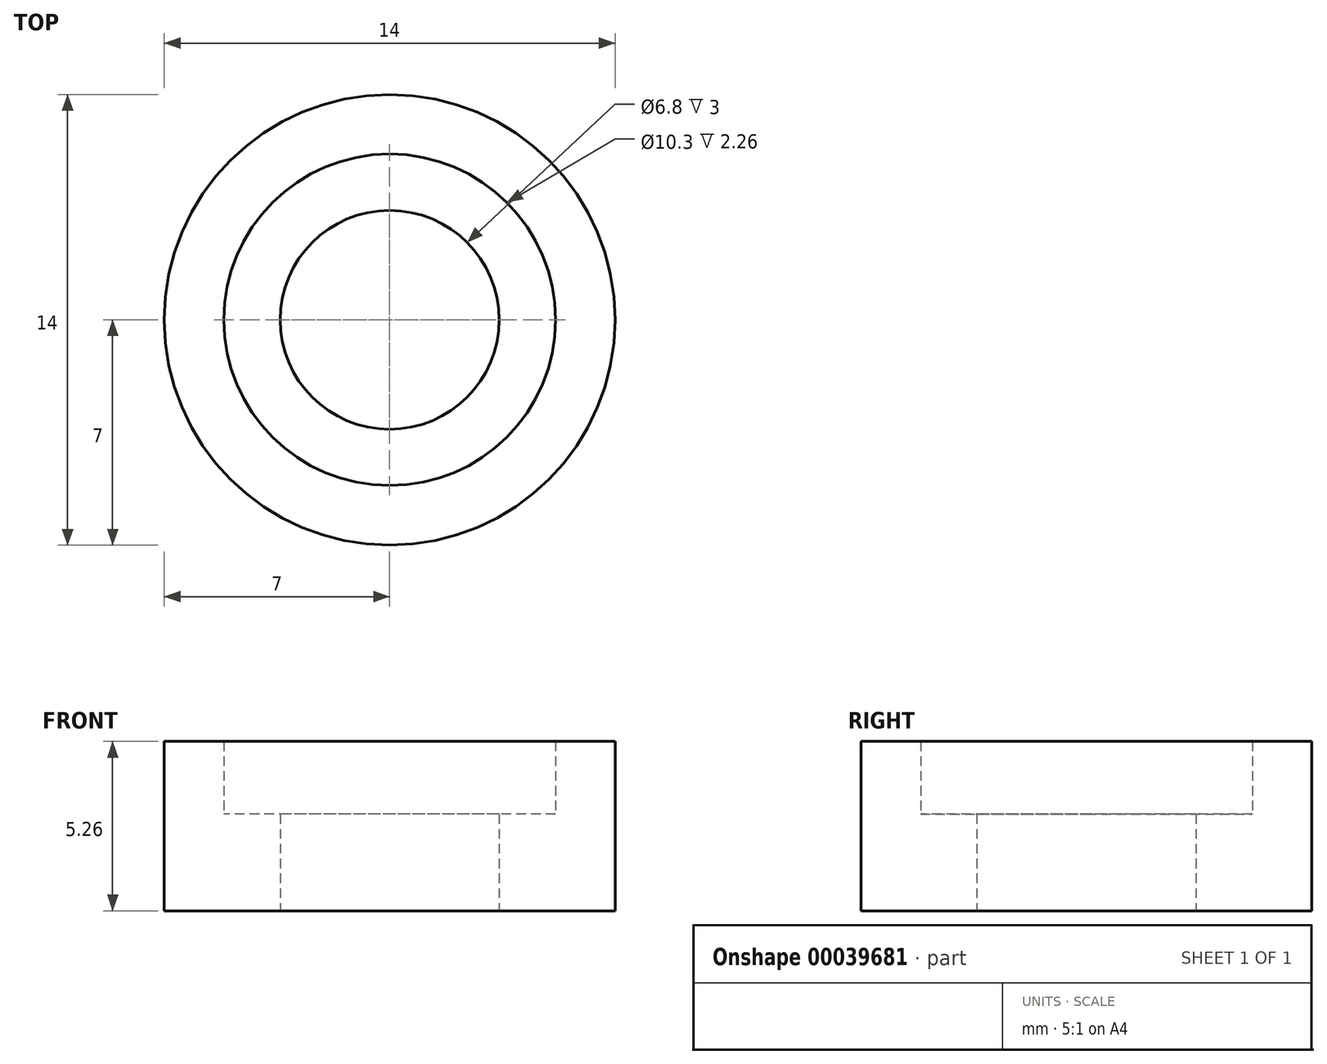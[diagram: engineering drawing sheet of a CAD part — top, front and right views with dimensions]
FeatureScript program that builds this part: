
annotation { "Feature Type Name" : "Feature", "Feature Type Description" : "" }
export const myFeature = defineFeature(function(context is Context, id is Id, definition is map)
    precondition{}
    {
        {
            var Q0;
            Q0=qCreatedBy(makeId("Top.planeOp"),FACE);
            var sketch = newSketch(context, id + "F0", { "sketchPlane" : qUnion([Q0])});
            skCircle(sketch, "E0", {"center": v(0, 0) * mm, "radius": 5.15 * mm});
            skCircle(sketch, "E1", {"center": v(0, 0) * mm, "radius": 7 * mm});
            skCircle(sketch, "E2", {"center": v(0, 0) * mm, "radius": 3.4 * mm});
            skSolve(sketch);
        }
        {
            var Q0;
            Q0=makeQuery(id+"F0.imprint","IMPRINT",FACE,{"disambiguationData":[TD([[makeQuery(id+"F0.imprint","IMPRINT",EDGE,{"derivedFrom":sQuery(id+"F0.wireOp",EDGE,"36c77d1d-454d-4323-b358-6101bc9ffe88")}),-1.0]])]});
            var Q1;
            Q1=makeQuery(id+"F0.imprint","IMPRINT",FACE,{"disambiguationData":[TD([[makeQuery(id+"F0.imprint","IMPRINT",EDGE,{"derivedFrom":sQuery(id+"F0.wireOp",EDGE,"E0")}),1.0]])]});
            extrude(context, id + "F1", {"entities" : qUnion([Q0, Q1]), "depth" : 3 * mm});
        }
        {
            var Q0;
            Q0=makeQuery(id+"F0.imprint","IMPRINT",FACE,{"disambiguationData":[TD([[makeQuery(id+"F0.imprint","IMPRINT",EDGE,{"derivedFrom":sQuery(id+"F0.wireOp",EDGE,"E0")}),-1.0]])]});
            extrude(context, id + "F2", {"entities" : qUnion([Q0]), "operationType" : NewBodyOperationType.ADD, "depth" : 5.26 * mm});
        }
    });
